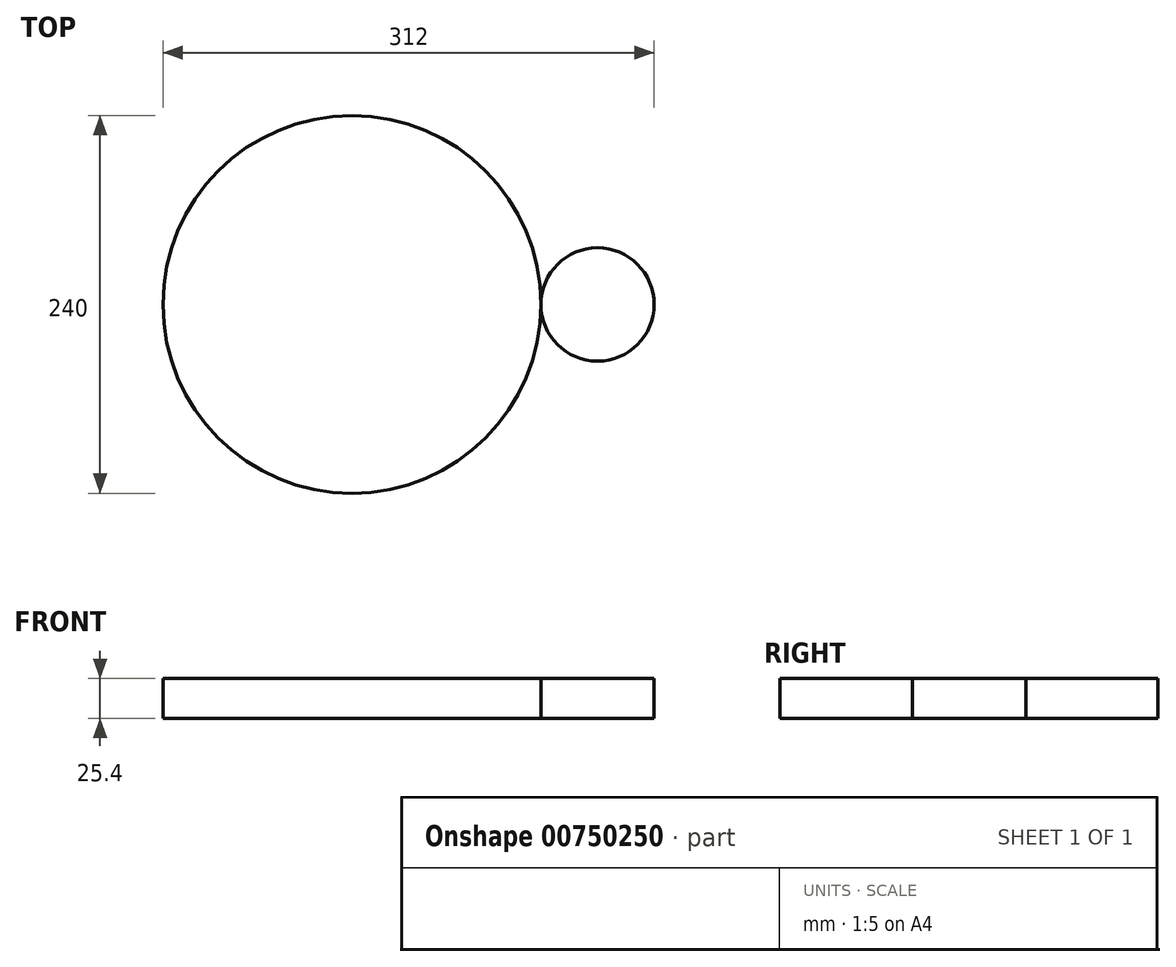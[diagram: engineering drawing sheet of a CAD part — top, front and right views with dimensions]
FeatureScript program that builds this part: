
annotation { "Feature Type Name" : "Feature", "Feature Type Description" : "" }
export const myFeature = defineFeature(function(context is Context, id is Id, definition is map)
    precondition{}
    {
        {
            var Q0;
            Q0=qCreatedBy(makeId("Top.planeOp"),FACE);
            var sketch = newSketch(context, id + "F0", { "sketchPlane" : qUnion([Q0])});
            skCircle(sketch, "E0", {"center": v(0, 0) * mm, "radius": 120 * mm});
            skLineSegment(sketch, "E1", {"start": v(0, 0) * mm, "end": v(120, 0) * mm});
            skLineSegment(sketch, "E2", {"start": v(120, 0) * mm, "end": v(156, 0) * mm});
            skCircle(sketch, "E3", {"center": v(156, 0) * mm, "radius": 36 * mm});
            skSolve(sketch);
        }
        {
            var Q0;
            Q0 = qSketchRegion(id + "F0", true);
            extrude(context, id + "F1", {"entities" : qUnion([Q0]), "depth" : 25.4 * mm, "offsetDistance" : 25.4 * mm});
        }
    });
